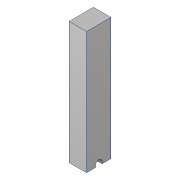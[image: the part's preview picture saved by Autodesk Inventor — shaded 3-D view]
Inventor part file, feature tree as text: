
AUTODESK INVENTOR PART (.ipt)
format: ipt  version: 2018 (Build 220112000, 112)  size: 114,688 bytes
history: native  units: mm
features: sketch x3, extrude x2, hole x1
ambient origin geometry x8: Origin, YZ Plane, XZ Plane, XY Plane, X Axis, Y Axis, Z Axis, Center Point
bodies: Solid1 (feature_tree)
feature tree (6):
  extrude  "Extrusion1"  Depth=60.0mm
  extrude  "Extrusion3"  Depth=16.0mm
  hole  "Hole1"  [1 undecoded]
  sketch  "Sketch1"  dims[d0=43.0mm d1=60.0mm]
  sketch  "Sketch4"  dims[d2=300.0mm d3=0.0mm d7=16.0mm]
  sketch  "Sketch5"  dims[d8=13.0mm d9=8.0mm d10=2.5mm d11=0.0mm d12=21.5mm d13=38.0mm d14=60.0mm d15=16.0mm d16=43.0mm d17=4.134mm d18=10.0mm d19=5.0mm d20=2.0mm d21=90.0deg d22=14.2mm d23=20.594885mm]
note: 1 required parameter value undecoded (feature->parameter linkage not recoverable at this tier; creation-order binding heuristic only, values carry confidence <= 0.55)
